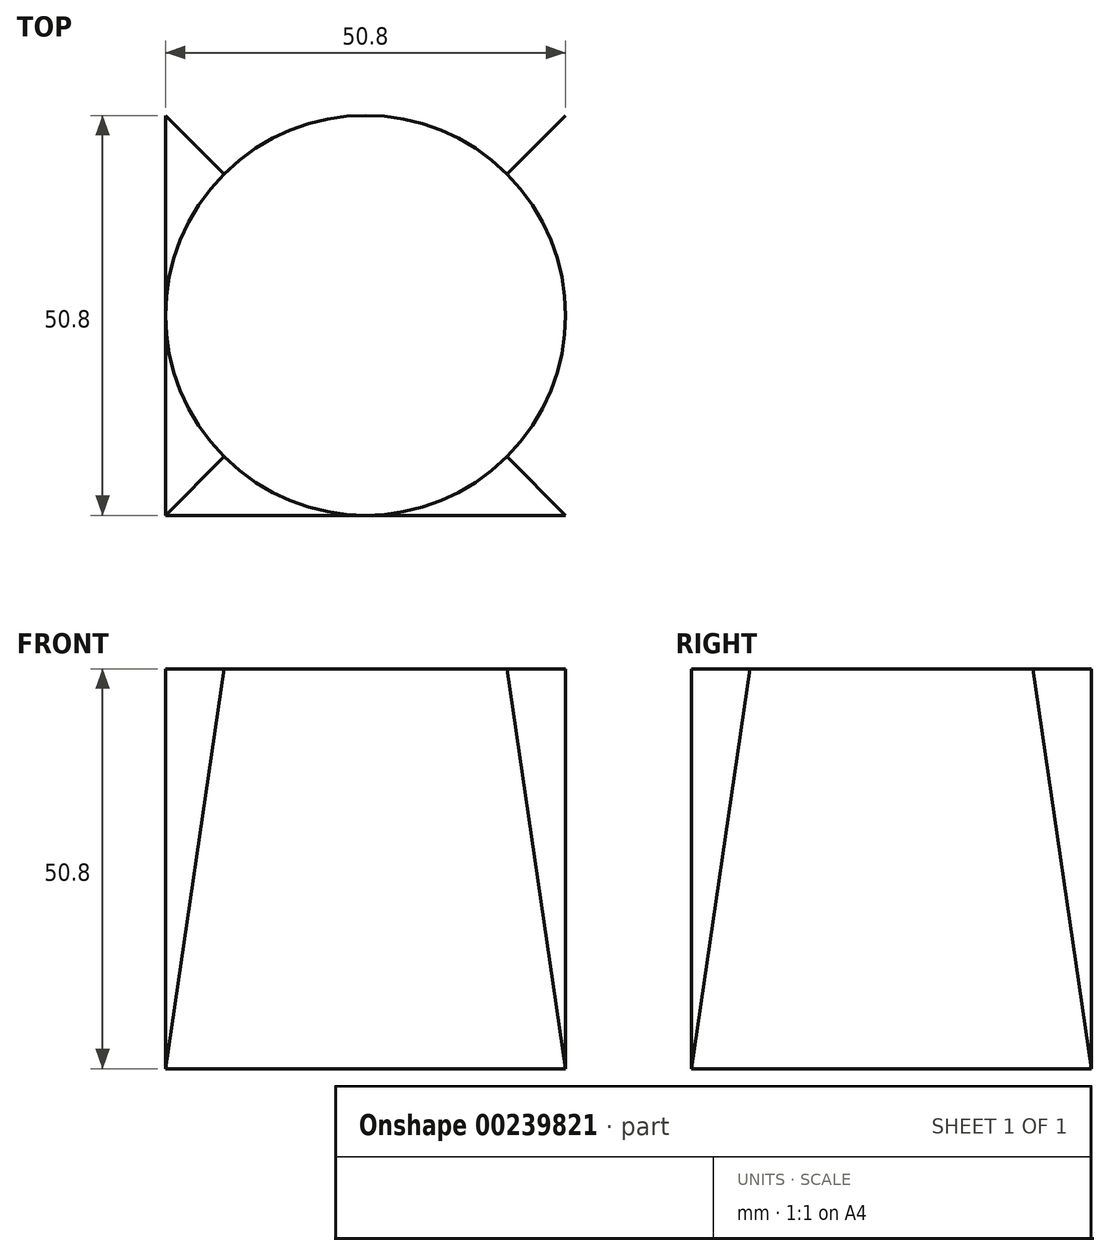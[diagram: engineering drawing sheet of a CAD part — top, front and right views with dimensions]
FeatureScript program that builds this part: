
annotation { "Feature Type Name" : "Feature", "Feature Type Description" : "" }
export const myFeature = defineFeature(function(context is Context, id is Id, definition is map)
    precondition{}
    {
        {
            var Q0;
            Q0=qCreatedBy(makeId("Top.planeOp"),FACE);
            var sketch = newSketch(context, id + "F0", { "sketchPlane" : qUnion([Q0])});
            skPoint(sketch, "E0.middle", {"position": v(0, 0) * mm});
            skLineSegment(sketch, "E1.bottom", {"start": v(25.4, 25.4) * mm, "end": v(-25.4, 25.4) * mm});
            skLineSegment(sketch, "E1.top", {"start": v(25.4, -25.4) * mm, "end": v(-25.4, -25.4) * mm});
            skLineSegment(sketch, "E1.left", {"start": v(25.4, 25.4) * mm, "end": v(25.4, -25.4) * mm});
            skLineSegment(sketch, "E1.right", {"start": v(-25.4, 25.4) * mm, "end": v(-25.4, -25.4) * mm});
            skSolve(sketch);
        }
        {
            var Q0;
            Q0=qCreatedBy(makeId("Top.planeOp"),FACE);
            cPlane(context, id + "F1", {"entities" : qUnion([Q0]), "cplaneType" : CPlaneType.OFFSET, "offset" : 50.8 * mm, "width" : 152.4 * mm, "height" : 152.4 * mm});
        }
        {
            var Q0;
            Q0=qCreatedBy(id+"F1.planeOp",FACE);
            var sketch = newSketch(context, id + "F2", { "sketchPlane" : qUnion([Q0])});
            skCircle(sketch, "E2", {"center": v(0, 0) * mm, "radius": 25.4 * mm});
            skSolve(sketch);
        }
        {
            var Q0;
            Q0=makeQuery(id+"F0.imprint","IMPRINT",FACE,{"disambiguationData":[TD([[makeQuery(id+"F0.imprint","IMPRINT",EDGE,{"derivedFrom":sQuery(id+"F0.wireOp",EDGE,"E1.bottom")}),1.0]])]});
            var Q1;
            Q1=makeQuery(id+"F2.imprint","IMPRINT",FACE,{"disambiguationData":[TD([[makeQuery(id+"F2.imprint","IMPRINT",EDGE,{"derivedFrom":sQuery(id+"F2.wireOp",EDGE,"E2")}),1.0]])]});
            loft(context, id + "F3", {"sheetProfilesArray" : [{ "sheetProfileEntities" : qUnion([Q0]) }, { "sheetProfileEntities" : qUnion([Q1]) }]});
        }
    });
